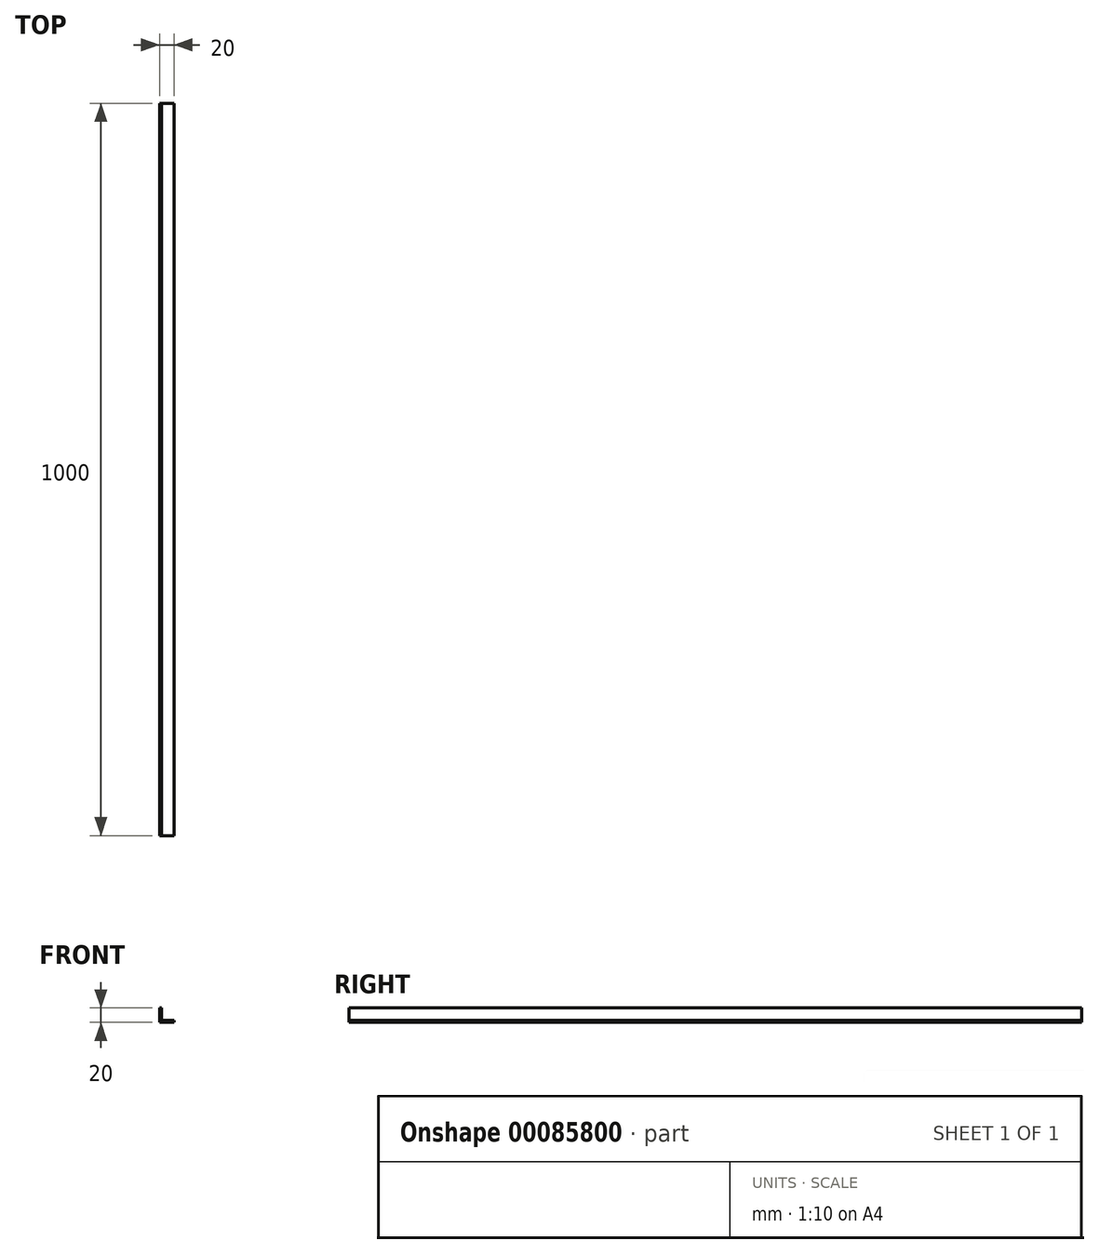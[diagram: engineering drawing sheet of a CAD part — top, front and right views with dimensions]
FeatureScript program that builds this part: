
annotation { "Feature Type Name" : "Feature", "Feature Type Description" : "" }
export const myFeature = defineFeature(function(context is Context, id is Id, definition is map)
    precondition{}
    {
        {
            var Q0;
            Q0=qCreatedBy(makeId("Front.planeOp"),FACE);
            var sketch = newSketch(context, id + "F0", { "sketchPlane" : qUnion([Q0])});
            skLineSegment(sketch, "E0", {"start": v(0, 0) * mm, "end": v(0, 20) * mm});
            skLineSegment(sketch, "E1", {"start": v(0, 20) * mm, "end": v(3, 20) * mm});
            skLineSegment(sketch, "E2", {"start": v(3, 20) * mm, "end": v(3, 3) * mm});
            skLineSegment(sketch, "E3", {"start": v(3, 3) * mm, "end": v(20, 3) * mm});
            skLineSegment(sketch, "E4", {"start": v(20, 3) * mm, "end": v(20, 0) * mm});
            skLineSegment(sketch, "E5", {"start": v(20, 0) * mm, "end": v(0, 0) * mm});
            skSolve(sketch);
        }
        {
            var Q0;
            Q0=makeQuery(id+"F0.imprint","IMPRINT",FACE,{"disambiguationData":[TD([[makeQuery(id+"F0.imprint","IMPRINT",EDGE,{"derivedFrom":sQuery(id+"F0.wireOp",EDGE,"E0")}),-1.0]])]});
            extrude(context, id + "F1", {"entities" : qUnion([Q0]), "depth" : 1000 * mm});
        }
    });
